# Revit family: Domotics-DomesticRanges-GEWISS-CHORUS_PROTECTION-SPD
name_source: partatom
category: Apparecchi elettrici
revit_build: Autodesk Revit 2016 (Build: 20161004_0715(x64)
units: mm (PartAtom-declared; Revit-internal decimal feet)

## family parameters
Condiviso = Sì
Host = Superficie
Mantenere orientamento annotazione = Sì
Punto di calcolo locali = Sì
Quota connettore circolare = Usa diametro
Taglio con vuoti quando caricato = Sì
Tipo di parte = Normale

## types (3) — shared parameters
Altezza_copriforo = 45 mm  [stored 0.147638 ft]
Catalogue = DOMOTICS
Catalogue Range = CHORUS - DOMESTIC RANGE
Description. = Limiter
Electrocod = 0142
IDF = 45043e9b-82ea-4c96-99d5-b507262a5122
IDT = 3d6990a7-eef1-4755-8e59-06db000df803
Immagine tipo = GW14492.jpg
Larghezza copriforo = 23 mm
No. Chorus modules = 1
No. Chorus modules: = 1
Produttore = GEWISS S.p.A.
Prospetto di default = 1219 mm
SEO = SPD
Technical sheet = https://www.gewiss.com
Tipo_ = CHORUS LIMITATORE TENSIONE : GW14492 Limitatore di sovratensioni 1M titanio
URL = https://www.gewiss.com
Uc = 275 V ac 50/60Hz
Up = 1 kV
Version file RFA = 19.0
Voltage = 230V ac
Voltage: = 230V ac
finitura = GEWISS TITANIO

## per-type parameters (varying)
| type | Colour | Descrizione | EAN code | Modello |
| GW12492 - Overvoltage limiter 1M black | Black | OVERVOLTAGE LIMITER 1M BLACK | 8011564268241 | GW12492 |
| GW10492 - Overvoltage limiter 1M white | White | OVERVOLTAGE LIMITER 1M WHITE | 8011564262911 | GW10492 |
| GW14492 - Overvoltage limiter, 1M titanium | Titanium | OVERVOLTAGE LIMITER, 1M TITANIUM | 8011564267831 | GW14492 |

note: [stored X ft] marks values corroborated as IEEE doubles in the binary element streams (Revit-internal decimal feet)

## geometry (parser evidence)
native form markers: Sweep x2
no freeform markers — native parametric forms only
